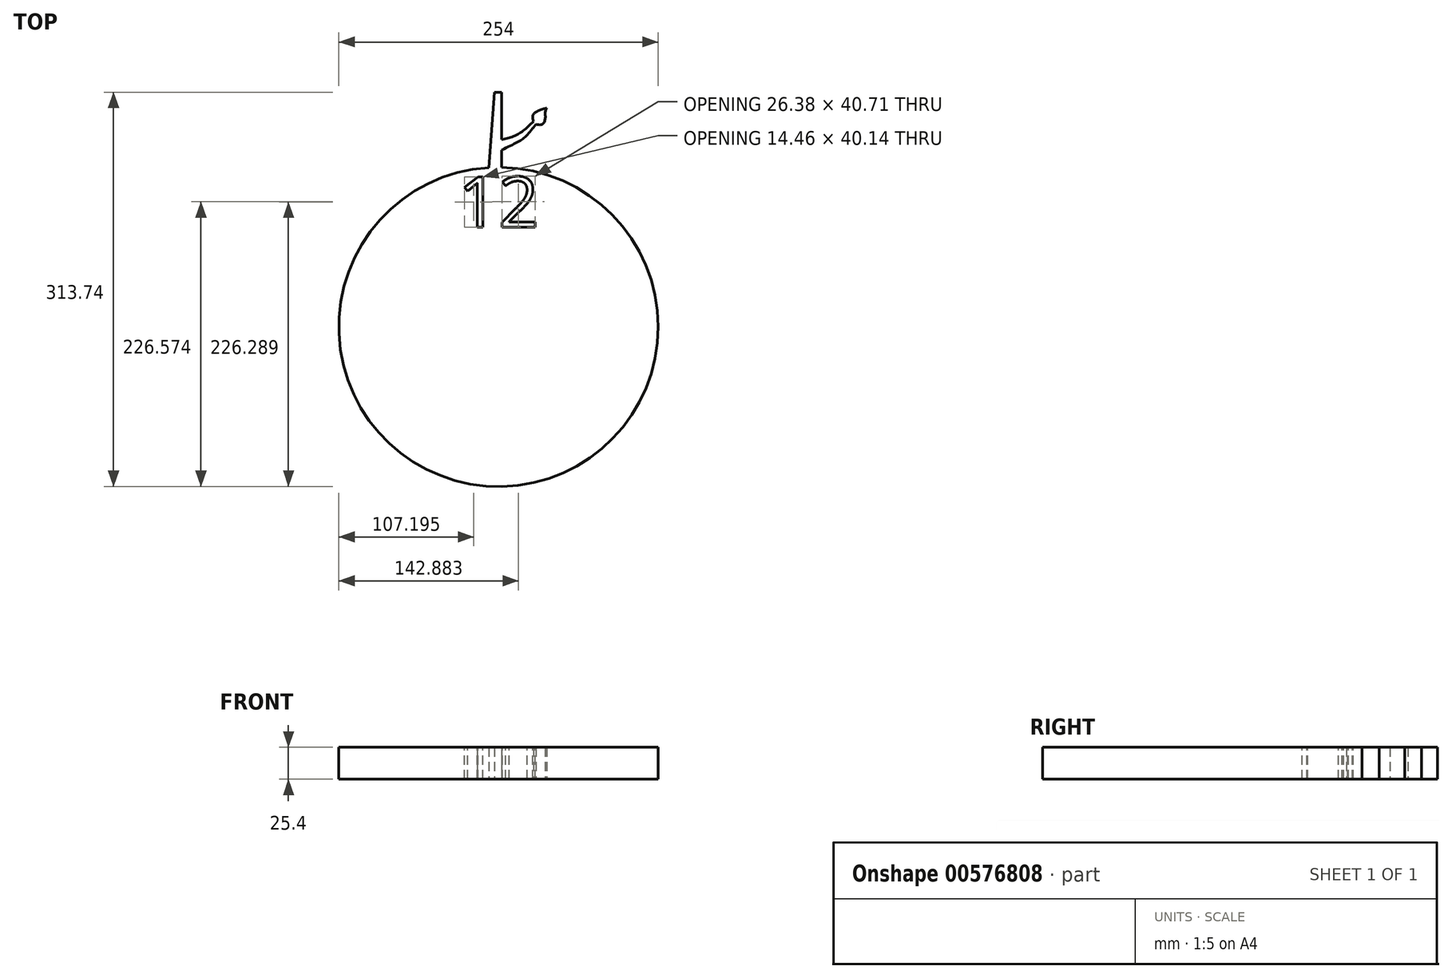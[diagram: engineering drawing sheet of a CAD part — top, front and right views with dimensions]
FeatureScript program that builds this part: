
annotation { "Feature Type Name" : "Feature", "Feature Type Description" : "" }
export const myFeature = defineFeature(function(context is Context, id is Id, definition is map)
    precondition{}
    {
        {
            var Q0;
            Q0=qCreatedBy(makeId("Top.planeOp"),FACE);
            var sketch = newSketch(context, id + "F0", { "sketchPlane" : qUnion([Q0])});
            skCircle(sketch, "E0", {"center": v(0, 0) * mm, "radius": 127 * mm});
            skSolve(sketch);
        }
        {
            var Q0;
            Q0=makeQuery(id+"F0.imprint","IMPRINT",FACE,{"disambiguationData":[TD([[makeQuery(id+"F0.imprint","IMPRINT",EDGE,{"derivedFrom":sQuery(id+"F0.wireOp",EDGE,"E0")}),1.0]])]});
            extrude(context, id + "F1", {"entities" : qUnion([Q0]), "depth" : 25.4 * mm, "offsetDistance" : 25.4 * mm});
        }
        {
            var Q0;
            Q0=qCreatedBy(makeId("Top.planeOp"),FACE);
            var sketch = newSketch(context, id + "F2", { "sketchPlane" : qUnion([Q0])});
            skLineSegment(sketch, "E1", {"start": v(-7.9, 125.92) * mm, "end": v(-3.27, 186.74) * mm});
            skLineSegment(sketch, "E2", {"start": v(-3.27, 186.74) * mm, "end": v(2.33, 186.74) * mm});
            skLineSegment(sketch, "E3", {"start": v(2.33, 186.74) * mm, "end": v(2.33, 125.16) * mm});
            skLineSegment(sketch, "E4", {"start": v(-7.9, 125.92) * mm, "end": v(2.33, 125.16) * mm});
            skSolve(sketch);
        }
        {
            var Q0;
            Q0=makeQuery(id+"F2.imprint","IMPRINT",FACE,{"disambiguationData":[TD([[makeQuery(id+"F2.imprint","IMPRINT",EDGE,{"derivedFrom":sQuery(id+"F2.wireOp",EDGE,"E1")}),-1.0]])]});
            extrude(context, id + "F3", {"entities" : qUnion([Q0]), "operationType" : NewBodyOperationType.ADD, "depth" : 25.4 * mm, "offsetDistance" : 25.4 * mm});
        }
        {
            var Q0;
            Q0=qCreatedBy(makeId("Top.planeOp"),FACE);
            var sketch = newSketch(context, id + "F4", { "sketchPlane" : qUnion([Q0])});
            skFitSpline(sketch, "E5", {"points": [v(2, 148.97) * mm, v(15.24, 153.15) * mm, v(27.78, 163.37) * mm], "startDerivative": vector(28.34, 6.05) * mm, "endDerivative": vector(23.28, 22.54) * mm});
            skFitSpline(sketch, "E6", {"points": [v(1.65, 140.26) * mm, v(15.82, 147.34) * mm, v(22.44, 152.34) * mm, v(29.75, 161.28) * mm], "startDerivative": vector(47.11, 24.02) * mm, "endDerivative": vector(19.5, 27.93) * mm});
            skFitSpline(sketch, "E7", {"points": [v(27.78, 163.37) * mm, v(27.78, 169.3) * mm, v(38.22, 174.1) * mm], "startDerivative": vector(-3.67, 15.25) * mm, "endDerivative": vector(22.67, 7.47) * mm});
            skFitSpline(sketch, "E8", {"points": [v(29.75, 161.28) * mm, v(34.86, 161.28) * mm, v(37.26, 166.36) * mm, v(38.22, 174.1) * mm], "startDerivative": vector(18.98, -5.13) * mm, "endDerivative": vector(13.65, 30.71) * mm});
            skFitSpline(sketch, "E9", {"points": [v(2, 148.97) * mm, v(1.65, 140.26) * mm], "startDerivative": vector(-0.35, -8.7) * mm, "endDerivative": vector(-0.35, -8.7) * mm});
            skSolve(sketch);
        }
        {
            var Q0;
            Q0=makeQuery(id+"F4.imprint","IMPRINT",FACE,{"disambiguationData":[TD([[makeQuery(id+"F4.imprint","IMPRINT",EDGE,{"derivedFrom":sQuery(id+"F4.wireOp",EDGE,"E5")}),-1.0]])]});
            extrude(context, id + "F5", {"entities" : qUnion([Q0]), "operationType" : NewBodyOperationType.ADD, "depth" : 25.4 * mm, "offsetDistance" : 25.4 * mm});
        }
        {
            var Q0;
            Q0=makeQuery(id+"F5.boolean.opBoolean","MERGE",FACE,{"derivedFrom":[makeQuery(id+"F3.boolean.opBoolean","MERGE",FACE,{"derivedFrom":[makeQuery(id+"F1.opExtrude","CAP_FACE",FACE,{"disambiguationData":[OSD([sQuery(id+"F0.wireOp",EDGE,"E0")])],"isStart":false}),makeQuery(id+"F3.opExtrude","CAP_FACE",FACE,{"disambiguationData":[OSD([sQuery(id+"F2.wireOp",EDGE,"E1"),sQuery(id+"F2.wireOp",EDGE,"E2"),sQuery(id+"F2.wireOp",EDGE,"E3"),sQuery(id+"F2.wireOp",EDGE,"E4")])],"isStart":false})]}),makeQuery(id+"F5.opExtrude","CAP_FACE",FACE,{"disambiguationData":[OSD([sQuery(id+"F4.wireOp",EDGE,"E5"),sQuery(id+"F4.wireOp",EDGE,"E6"),sQuery(id+"F4.wireOp",EDGE,"E7"),sQuery(id+"F4.wireOp",EDGE,"E8"),sQuery(id+"F4.wireOp",EDGE,"E9")])],"isStart":false})]});
            var sketch = newSketch(context, id + "F6", { "sketchPlane" : qUnion([Q0])});
            skText(sketch, "E10", { "text": "12", "fontName": "OpenSans-Regular.ttf"});
            const initialGuessF6  = {"E10": [-0.0322, 0.07922, 1, 0, 0.04048]};
            skSetInitialGuess(sketch, initialGuessF6);
            skSolve(sketch);
        }
        {
            var Q0;
            Q0 = qSketchRegion(id + "F6", true);
            extrude(context, id + "F7", {"entities" : qUnion([Q0]), "operationType" : NewBodyOperationType.REMOVE, "oppositeDirection" : true, "depth" : 50.8 * mm, "offsetDistance" : 25.4 * mm});
        }
    });
